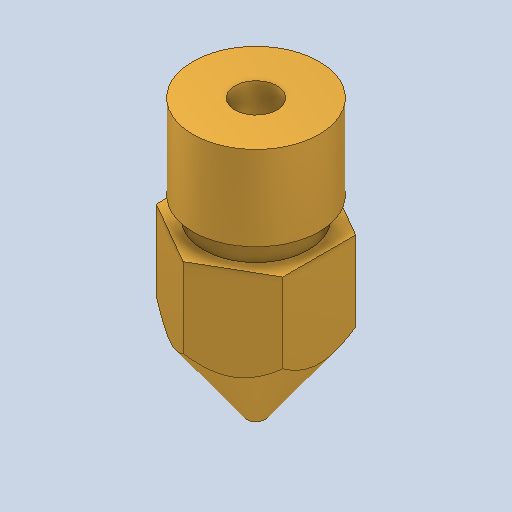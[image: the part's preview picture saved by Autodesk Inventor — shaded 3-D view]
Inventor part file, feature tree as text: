
AUTODESK INVENTOR PART (.ipt)
format: ipt  version: 2022 (Build 260153070, 153G)  size: 152,576 bytes
history: native  units: mm
features: sketch x2, revolve x1, extrude x1
ambient origin geometry x8: Origin, YZ Plane, XZ Plane, XY Plane, X Axis, Y Axis, Z Axis, Center Point
bodies: Solid1 (feature_tree)
feature tree (4):
  revolve  "Revolution1"  [1 undecoded]
  extrude  "Extrusion1"  Depth=6.0mm
  sketch  "Sketch1"  dims[d0=3.0mm d1=13.0mm]
  sketch  "Sketch2"  dims[d2=9.0mm d5=0.45mm d6=2.5mm d7=45.0deg d8=1.0mm d9=0.2mm d10=0.8mm d11=90.0deg d12=3.57735mm d13=8.0mm d14=6.195919mm d15=6.0mm d17=10.0mm d18=8.0mm d19=0.0mm]
note: 1 required parameter value undecoded (feature->parameter linkage not recoverable at this tier; creation-order binding heuristic only, values carry confidence <= 0.55)
